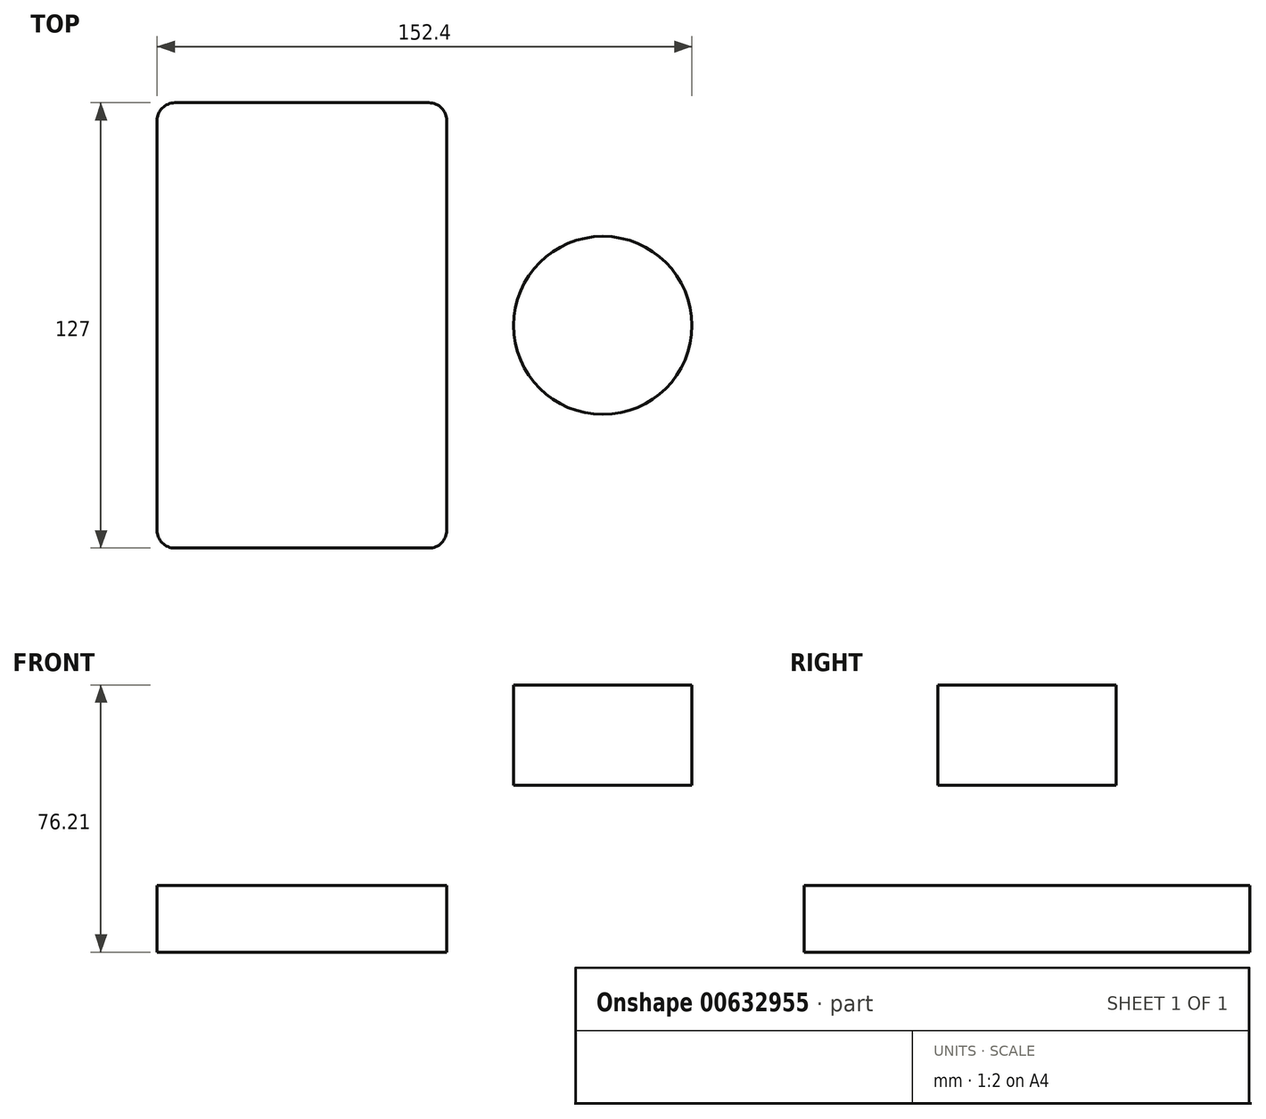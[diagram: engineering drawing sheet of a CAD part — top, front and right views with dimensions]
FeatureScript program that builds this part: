
annotation { "Feature Type Name" : "Feature", "Feature Type Description" : "" }
export const myFeature = defineFeature(function(context is Context, id is Id, definition is map)
    precondition{}
    {
        {
            var Q0;
            Q0=qCreatedBy(makeId("Front.planeOp"),FACE);
            var sketch = newSketch(context, id + "F0", { "sketchPlane" : qUnion([Q0])});
            skLineSegment(sketch, "E0.rect.bottom", {"start": v(-41.28, 9.52) * mm, "end": v(41.28, 9.52) * mm});
            skLineSegment(sketch, "E0.rect.top", {"start": v(-41.28, -9.52) * mm, "end": v(41.28, -9.52) * mm});
            skLineSegment(sketch, "E0.rect.left", {"start": v(-41.28, 9.52) * mm, "end": v(-41.28, -9.52) * mm});
            skLineSegment(sketch, "E0.rect.right", {"start": v(41.28, 9.52) * mm, "end": v(41.28, -9.52) * mm});
            skPoint(sketch, "E0.rect.middle", {"position": v(0, 0) * mm});
            skLineSegment(sketch, "E1", {"start": v(41.28, 9.52) * mm, "end": v(41.28, 27) * mm});
            skArc(sketch, "E2", {"start": v(41.28, 27) * mm, "mid": v(45.92, 38.23) * mm, "end": v(57.15, 42.88) * mm});
            skLineSegment(sketch, "E3", {"start": v(57.15, 42.88) * mm, "end": v(85.72, 42.88) * mm});
            skLineSegment(sketch, "E4.rect.bottom", {"start": v(60.32, 38.1) * mm, "end": v(111.12, 38.1) * mm});
            skLineSegment(sketch, "E4.rect.top", {"start": v(60.32, 66.68) * mm, "end": v(111.12, 66.68) * mm});
            skLineSegment(sketch, "E4.rect.left", {"start": v(60.32, 38.1) * mm, "end": v(60.32, 66.68) * mm});
            skLineSegment(sketch, "E4.rect.right", {"start": v(111.13, 38.1) * mm, "end": v(111.12, 66.68) * mm});
            skPoint(sketch, "E4.rect.middle", {"position": v(85.72, 52.39) * mm});
            skLineSegment(sketch, "E5.0", {"start": v(57.15, 61.93) * mm, "end": v(85.72, 61.93) * mm});
            skArc(sketch, "E5.1", {"start": v(22.23, 27) * mm, "mid": v(32.45, 51.7) * mm, "end": v(57.15, 61.93) * mm});
            skLineSegment(sketch, "E5.2", {"start": v(22.23, 9.52) * mm, "end": v(22.23, 27) * mm});
            skLineSegment(sketch, "E6", {"start": v(85.72, 38.1) * mm, "end": v(85.72, 66.68) * mm});
            skFitSpline(sketch, "E7", {"points": [v(-41.28, 9.53) * mm, v(57.15, 61.93) * mm], "startDerivative": vector(5.2, 92.34) * mm, "endDerivative": vector(120.92, 4.22) * mm});
            skSolve(sketch);
        }
        {
            var Q0;
            Q0=makeQuery(id+"F0.imprint","IMPRINT",FACE,{"disambiguationData":[TD([[makeQuery(id+"F0.imprint","IMPRINT",EDGE,{"derivedFrom":sQuery(id+"F0.wireOp",EDGE,"E0.rect.top")}),1.0]])]});
            extrude(context, id + "F1", {"entities" : qUnion([Q0]), "depth" : 127 * mm, "symmetric" : true});
        }
        {
            var Q0;
            {var subQ5=sQuery(id+"F0.wireOp",EDGE,"E4.rect.right");Q0=makeQuery(id+"F0.imprint","IMPRINT",FACE,{"disambiguationData":[TD([[makeQuery(id+"F0.imprint","IMPRINT",EDGE,{"derivedFrom":subQ5}),1.0]])]});}
            var Q1;
            Q1=sQuery(id+"F0.wireOp",EDGE,"E6");
            revolve(context, id + "F2", {"operationType" : NewBodyOperationType.ADD, "entities" : qUnion([Q0]), "axis" : qUnion([Q1]), "revolveType" : RevolveType.FULL});
        }
        {
            var Q0;
            Q0=makeQuery(id+"F1.opExtrude","CAP_EDGE",EDGE,{"disambiguationData":[OSD([sQuery(id+"F0.wireOp",EDGE,"E0.rect.right")])],"isStart":false});
            var Q1;
            Q1=makeQuery(id+"F1.opExtrude","CAP_EDGE",EDGE,{"disambiguationData":[OSD([sQuery(id+"F0.wireOp",EDGE,"E0.rect.left")])],"isStart":false});
            var Q2;
            Q2=makeQuery(id+"F1.opExtrude","CAP_EDGE",EDGE,{"disambiguationData":[OSD([sQuery(id+"F0.wireOp",EDGE,"E0.rect.right")])],"isStart":true});
            var Q3;
            Q3=makeQuery(id+"F1.opExtrude","CAP_EDGE",EDGE,{"disambiguationData":[OSD([sQuery(id+"F0.wireOp",EDGE,"E0.rect.left")])],"isStart":true});
            fillet(context, id + "F3", {"entities" : qUnion([Q0, Q1, Q2, Q3]), "radius" : 5.08 * mm, "tangentPropagation" : true, "allowEdgeOverflow" : false});
        }
    });
